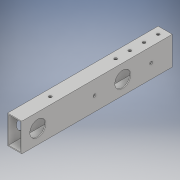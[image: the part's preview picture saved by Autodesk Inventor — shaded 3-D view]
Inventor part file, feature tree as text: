
AUTODESK INVENTOR PART (.ipt)
format: ipt  version: 2018 (Build 220112000, 112)  size: 153,600 bytes
history: native  units: in
note: dims shown in document units (in); Inventor stores cm internally (conversion verified against a paired STEP export)
features: extrude x6, sketch x6
ambient origin geometry x8: Origin, YZ Plane, XZ Plane, XY Plane, X Axis, Y Axis, Z Axis, Center Point
bodies: Solid1 (feature_tree)
feature tree (12):
  extrude  "Extrusion1"  Depth=2.0in
  sketch  "Sketch2"  dims[d2=0.0625in d3=10.625in d4=0.0in]
  extrude  "Extrusion4"  Depth=10.625in TaperAngle=0.0deg
  extrude  "Extrusion5"  Depth=1.0in
  extrude  "Extrusion7"  Depth=1.0in
  extrude  "Extrusion9"  Depth=1.125in
  extrude  "Extrusion10"  Depth=1.0in TaperAngle=0.0deg
  sketch  "Sketch1"  dims[d0=1.0in d1=2.0in]
  sketch  "Sketch4"  dims[d14=0.5in d15=1.0in]
  sketch  "Sketch5"  dims[d16=1.0in d17=0.2031in]
  sketch  "Sketch7"  dims[d18=2.6875in d19=0.0in d20=1.125in]
  sketch  "Sketch8"  dims[d21=1.125in d22=1.0in d23=0.0in d24=1.5in d25=180.0deg d26=4.0in d27=0.2031in d30=1.125in d31=1.0in d32=0.0in d37=1.0in d38=2.625in d39=0.0in d40=2.5in d41=0.2031in d42=2.625in d43=0.0in]
